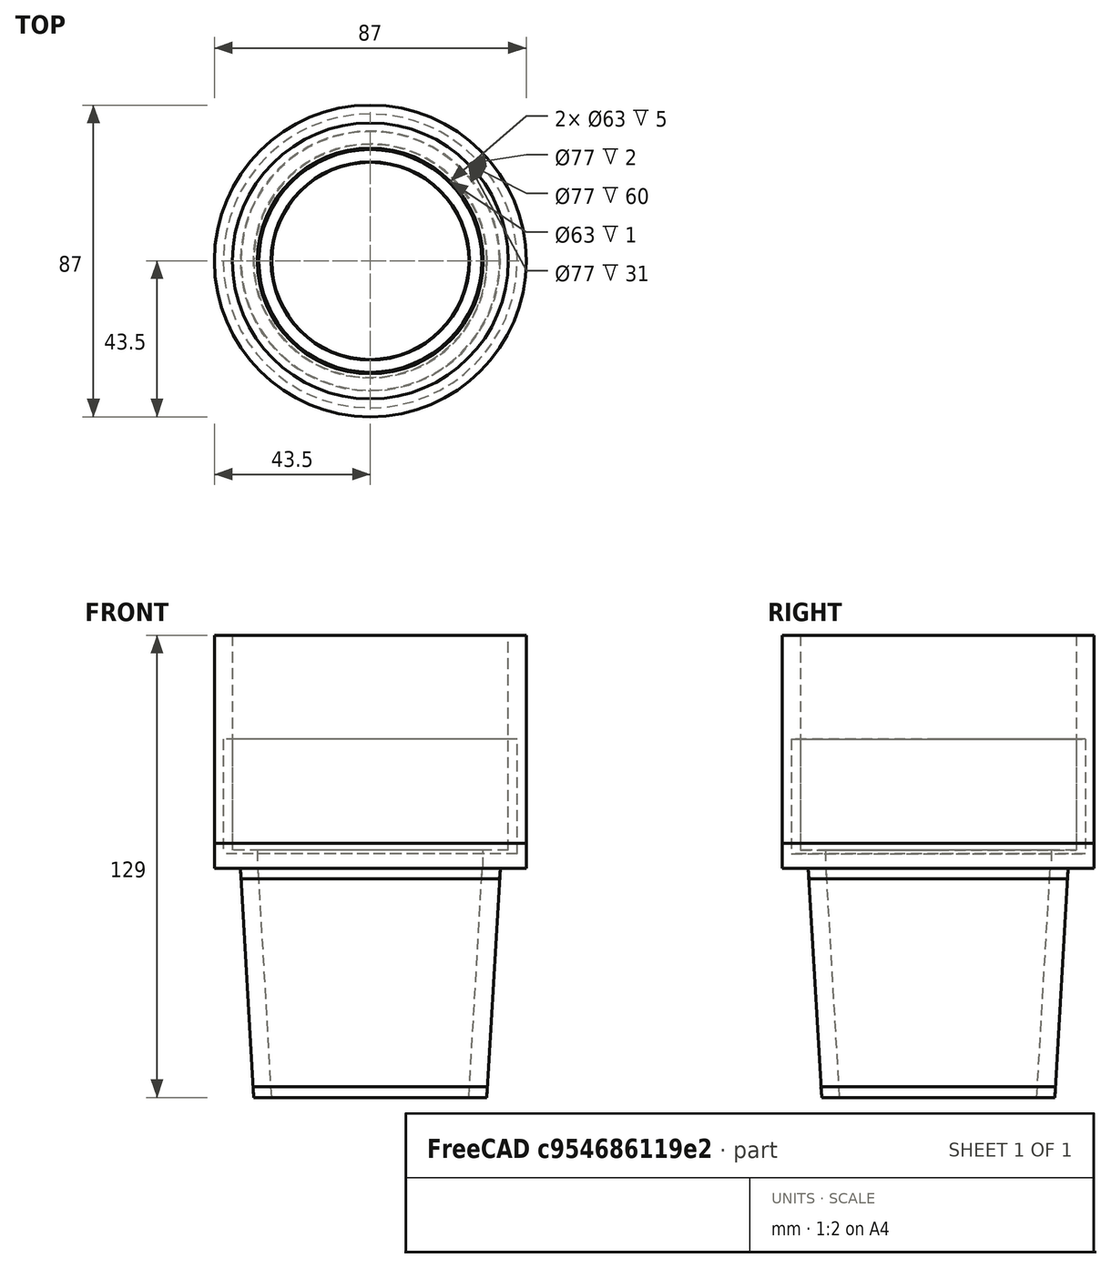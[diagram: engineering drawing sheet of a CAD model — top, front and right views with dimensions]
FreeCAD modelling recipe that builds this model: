
FCSTD DOCUMENT  (FreeCAD 1.1R20260325 (Git shallow))
Label: porta_botella
License: All rights reserved
LicenseURL: https://en.wikipedia.org/wiki/All_rights_reserved
objects: Part::Cut×10, Part::Cylinder×6, Part::Box×5, Mesh::Feature×4, Part::Feature×3, Part::Cone×2, Part::MultiFuse×1, Measure::MeasureDistance×1
note: 27 computed .brp shape members not serialized (recipe doc carries the construction recipe); baked Part::Feature solids carry a one-line shape summary decoded from their .brp

FEATURE [Part::Cylinder] Cylinder  label="Interior_cilindor"
  Angle = 360
  AttacherType = Attacher::AttachEngine3D
  FirstAngle = 0
  Height = 60
  Radius = 38.5
  SecondAngle = 0
FEATURE [Part::Cylinder] Cylinder001  label="Exterior_cilindro"
  Angle = 360
  AttacherType = Attacher::AttachEngine3D
  FirstAngle = 0
  Height = 60
  Radius = 43.5
  SecondAngle = 0
FEATURE [Part::Cut] Cut  label="Cilindro_superior"
  Base = -> Cylinder001
  Placement = pos=(0,0,69) rot=(0,0,1;0rad)
  Refine = true
  Tool = -> Cylinder
FEATURE [Part::Cone] Cone  label="Interior_cono"
  Angle = 360
  AttacherType = Attacher::AttachEngine3D
  Height = 64
  Radius1 = 27.5
  Radius2 = 31.25
FEATURE [Part::Cone] Cone001  label="Exterior_Cono"
  Angle = 360
  AttacherType = Attacher::AttachEngine3D
  Height = 64
  Radius1 = 32.5
  Radius2 = 36.25
FEATURE [Part::Cut] Cut001  label="Cono_inferior"
  Base = -> Cone001
  Refine = true
  Tool = -> Cone
FEATURE [Part::Cylinder] Cylinder002  label="Interior_cilindor001"
  Angle = 360
  AttacherType = Attacher::AttachEngine3D
  FirstAngle = 0
  Height = 5
  Radius = 31.5
  SecondAngle = 0
FEATURE [Part::Cylinder] Cylinder003  label="Exterior_cilindro001"
  Angle = 360
  AttacherType = Attacher::AttachEngine3D
  FirstAngle = 0
  Height = 5
  Radius = 43.5
  SecondAngle = 0
FEATURE [Part::Cut] Cut002  label="Anillo_Union"
  Base = -> Cylinder003
  Placement = pos=(0,0,64) rot=(0,0,1;0rad)
  Refine = true
  Tool = -> Cylinder002
FEATURE [Part::MultiFuse] Fusion  label="Parte"
  Refine = true
  Shapes = -> [Cut,Cut001,Cut002]
FEATURE [Part::Feature] Fusion001  label="para_test_botella_cono_superior"
  shape: bbox 87 x 87 x 129 mm, 10 faces (baked)
FEATURE [Part::Feature] Fusion003  label="para_test_cono_inferior"
  shape: bbox 87 x 87 x 129 mm, 10 faces (baked)
FEATURE [Part::Box] Box  label="Cube"
  AttacherType = Attacher::AttachEngine3D
  Height = 100
  Length = 120
  Placement = pos=(-60,-60,71) rot=(0,0,1;0rad)
  Width = 120
FEATURE [Part::Box] Box001  label="Cube001"
  AttacherType = Attacher::AttachEngine3D
  Height = 100
  Length = 120
  Placement = pos=(-60,-60,-39) rot=(0,0,1;0rad)
  Width = 120
FEATURE [Part::Cut] Cut003
  Base = -> Fusion001
  Refine = true
  Tool = -> Box
FEATURE [Part::Cut] Cut004  label="Test_botella_cono_superior"
  Base = -> Cut003
  Refine = true
  Tool = -> Box001
FEATURE [Part::Box] Box002  label="Cube002"
  AttacherType = Attacher::AttachEngine3D
  Height = 200
  Length = 120
  Placement = pos=(-60,-60,3) rot=(0,0,1;0rad)
  Width = 120
FEATURE [Part::Cut] Cut005  label="test_cono_inferior"
  Base = -> Fusion003
  Refine = true
  Tool = -> Box002
FEATURE [Mesh::Feature] Mesh  label="Test_botella_cono_superior (Meshed)"
FEATURE [Mesh::Feature] Mesh001  label="test_cono_inferior (Meshed)"
FEATURE [Mesh::Feature] Mesh002  label="Parte (Meshed)"
FEATURE [Part::Box] Box003  label="Cube003"
  AttacherType = Attacher::AttachEngine3D
  Height = 100
  Length = 120
  Placement = pos=(-60,-60,100) rot=(0,0,1;0rad)
  Width = 120
FEATURE [Part::Box] Box004  label="Cube004"
  AttacherType = Attacher::AttachEngine3D
  Height = 100
  Length = 120
  Placement = pos=(-60,-60,-32) rot=(0,0,1;0rad)
  Width = 120
FEATURE [Part::Feature] Fusion004  label="para_test_botella_cono_superior001"
  shape: bbox 87 x 87 x 129 mm, 10 faces (baked)
FEATURE [Part::Cut] Cut006
  Base = -> Fusion004
  Refine = true
  Tool = -> Box003
FEATURE [Part::Cut] Cut007
  Base = -> Cut006
  Refine = true
  Tool = -> Box004
FEATURE [Part::Cylinder] Cylinder004  label="Cylinder"
  Angle = 360
  AttacherType = Attacher::AttachEngine3D
  FirstAngle = 0
  Height = 106
  Radius = 41
  SecondAngle = 0
FEATURE [Part::Cylinder] Cylinder005
  Angle = 360
  AttacherType = Attacher::AttachEngine3D
  FirstAngle = 0
  Height = 106
  Radius = 48
  SecondAngle = 0
FEATURE [Part::Cut] Cut008
  Base = -> Cylinder005
  Refine = true
  Tool = -> Cylinder004
FEATURE [Part::Cut] Cut009
  Base = -> Cut007
  Refine = true
  Tool = -> Cut008
FEATURE [Mesh::Feature] Mesh003  label="Cut009 (Meshed)"
FEATURE [Measure::MeasureDistance] Distance  label="Distance: 60.00 mm"
  Distance = 60
  DistanceX = 0
  DistanceY = 0
  DistanceZ = 60
  Element1 = -> Fusion [Edge4]
  Element2 = -> Fusion [Edge2]
  Position1 = (0,0,69)
  Position2 = (0,0,129)
